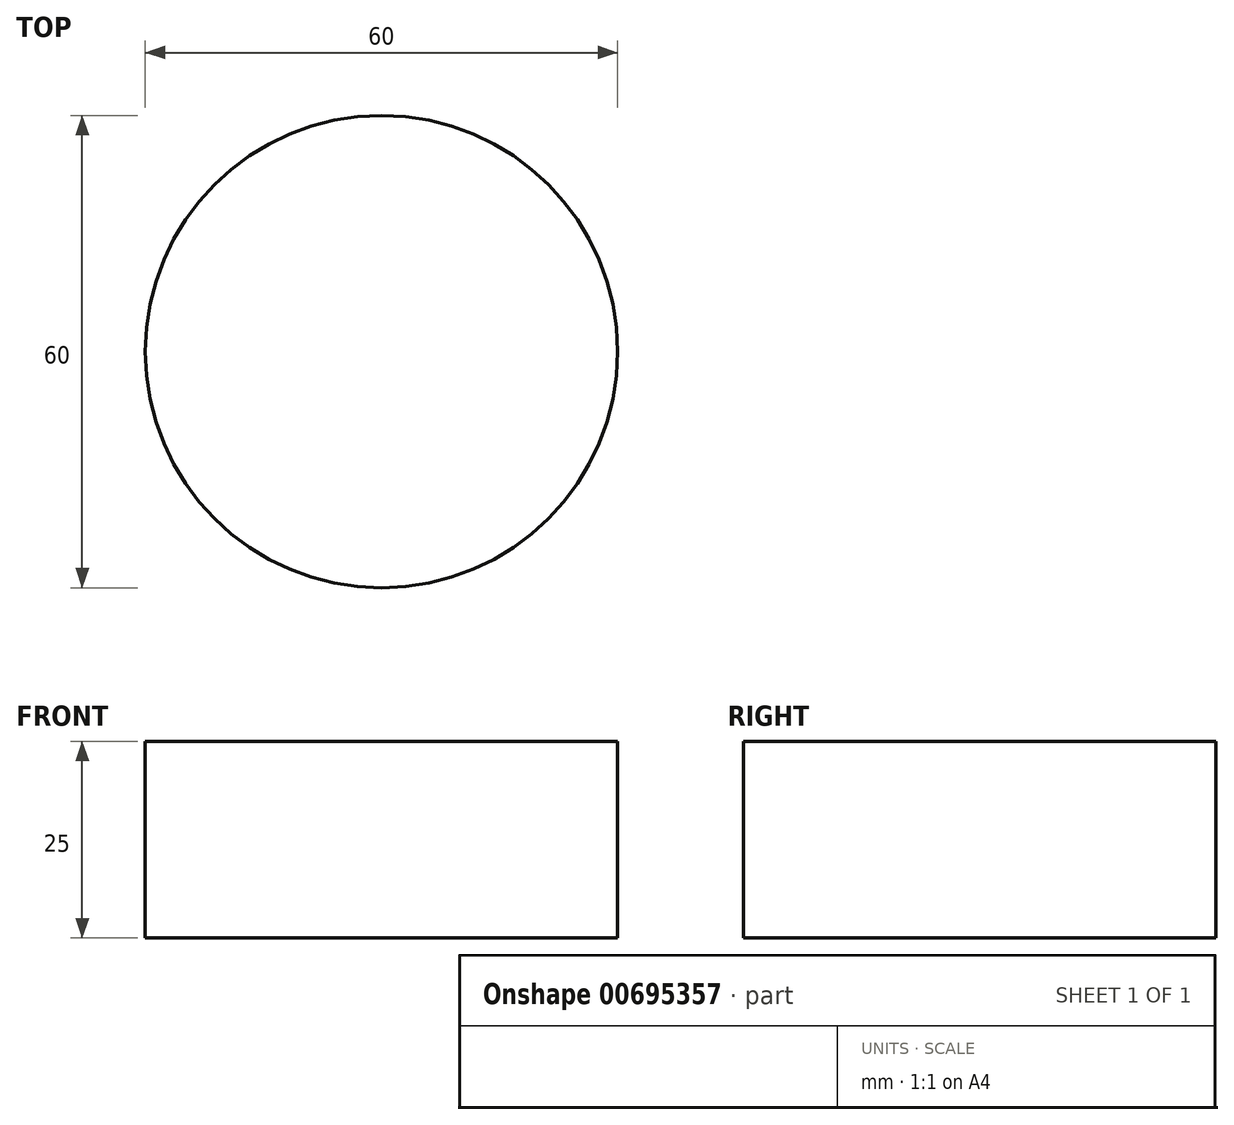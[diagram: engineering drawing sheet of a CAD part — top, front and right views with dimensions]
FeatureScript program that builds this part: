
annotation { "Feature Type Name" : "Feature", "Feature Type Description" : "" }
export const myFeature = defineFeature(function(context is Context, id is Id, definition is map)
    precondition{}
    {
        {
            var Q0;
            Q0=qCreatedBy(makeId("Top.planeOp"),FACE);
            var sketch = newSketch(context, id + "F0", { "sketchPlane" : qUnion([Q0])});
            skCircle(sketch, "E0", {"center": v(-9.53, 12.79) * mm, "radius": 30 * mm});
            skSolve(sketch);
        }
        {
            var Q0;
            Q0=makeQuery(id+"F0.imprint","IMPRINT",FACE,{"disambiguationData":[TD([[makeQuery(id+"F0.imprint","IMPRINT",EDGE,{"derivedFrom":sQuery(id+"F0.wireOp",EDGE,"E0")}),1.0]])]});
            extrude(context, id + "F1", {"entities" : qUnion([Q0]), "depth" : 25 * mm, "offsetDistance" : 25 * mm});
        }
    });
